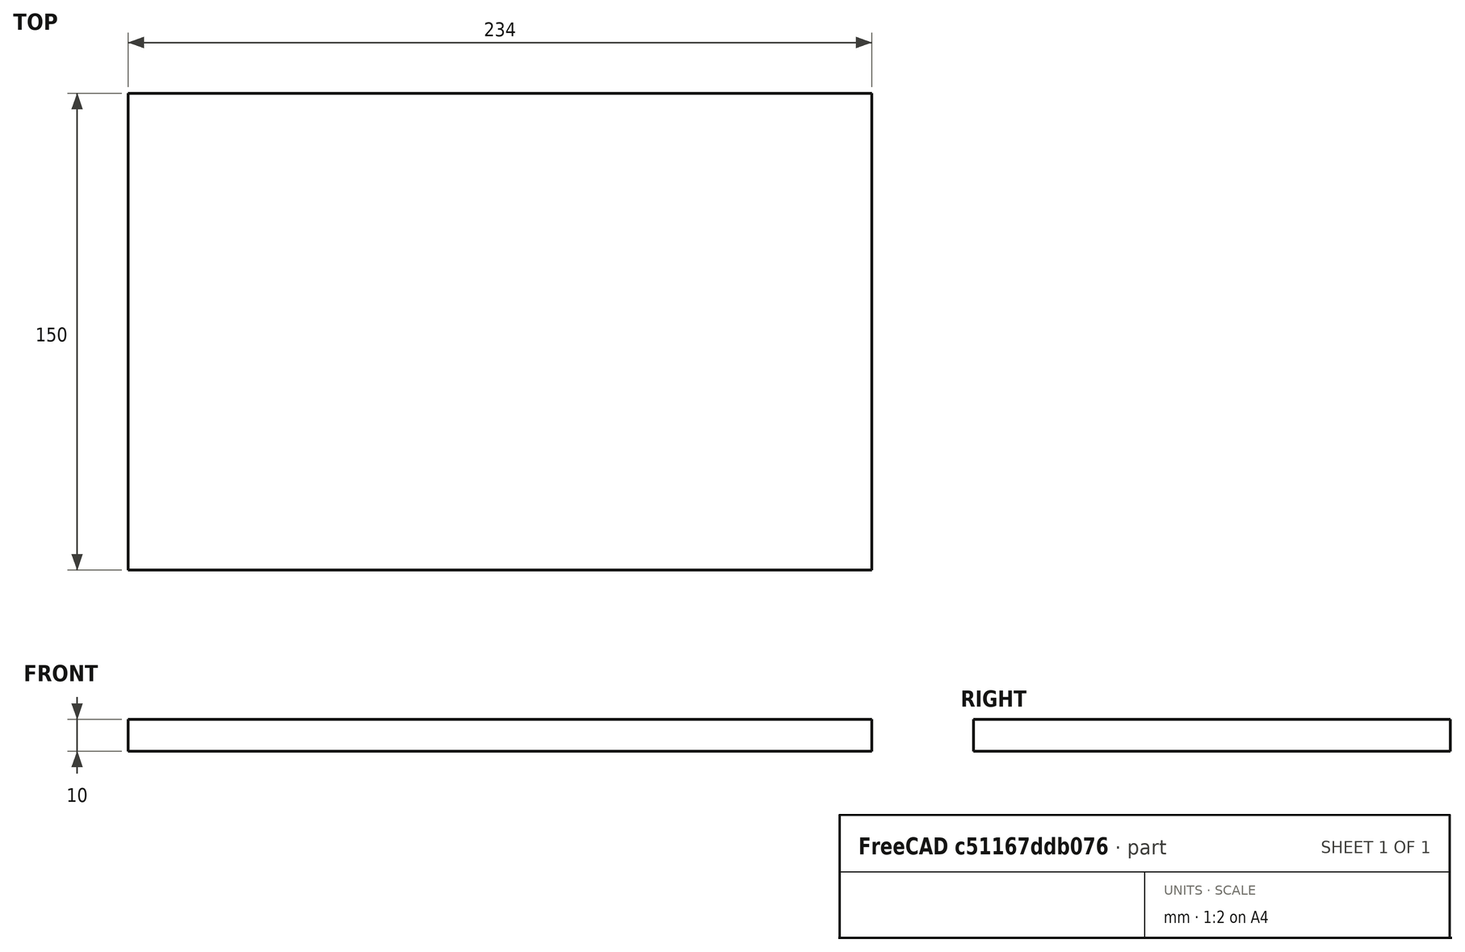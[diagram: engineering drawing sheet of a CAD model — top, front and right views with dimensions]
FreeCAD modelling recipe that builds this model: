
FCSTD DOCUMENT  (FreeCAD 1.0R39319 (Git))
Label: comp22A_16mm_plate.py
License: All rights reserved
LicenseURL: https://en.wikipedia.org/wiki/All_rights_reserved
objects: Sketcher::SketchObject×1, PartDesign::Pad×1, PartDesign::Body×1
note: 6 computed .brp shape members not serialized (recipe doc carries the construction recipe); baked Part::Feature solids carry a one-line shape summary decoded from their .brp

FEATURE [Sketcher::SketchObject] Sketch
  ArcFitTolerance = 1e-06
  AttachmentSupport = -> [XY_Plane]
  FullyConstrained = true
  MakeInternals = false
  MapMode = 5
  sketch-geometry (4):
    g0: LineSegment StartX=0 StartY=150 StartZ=0 EndX=0 EndY=0 EndZ=0
    g1: LineSegment StartX=0 StartY=0 StartZ=0 EndX=234 EndY=0 EndZ=0
    g2: LineSegment StartX=234 StartY=0 StartZ=0 EndX=234 EndY=150 EndZ=0
    g3: LineSegment StartX=234 StartY=150 StartZ=0 EndX=0 EndY=150 EndZ=0
  constraints (11):
    c: Coincident(g0,g1)
    c: Coincident(g1,g2)
    c: Coincident(g2,g3)
    c: Coincident(g3,g0)
    c: Vertical(g0)
    c: Vertical(g2)
    c: Horizontal(g1)
    c: Horizontal(g3)
    c: DistanceY(g0,g0) = 150
    c: DistanceX(g1,g1) = 234
    c: Coincident(g0,g-1)
FEATURE [PartDesign::Pad] Pad
  Direction = (0,0,1)
  Length = 10
  Length2 = 10
  Profile = -> Sketch
  ReferenceAxis = -> Sketch [N_Axis]
  Refine = true
  Suppressed = false
  Type = 0
FEATURE [PartDesign::Body] Body
  AllowCompound = false
  Group = -> [Sketch,Pad]
  Origin = -> Origin
  Tip = -> Pad
